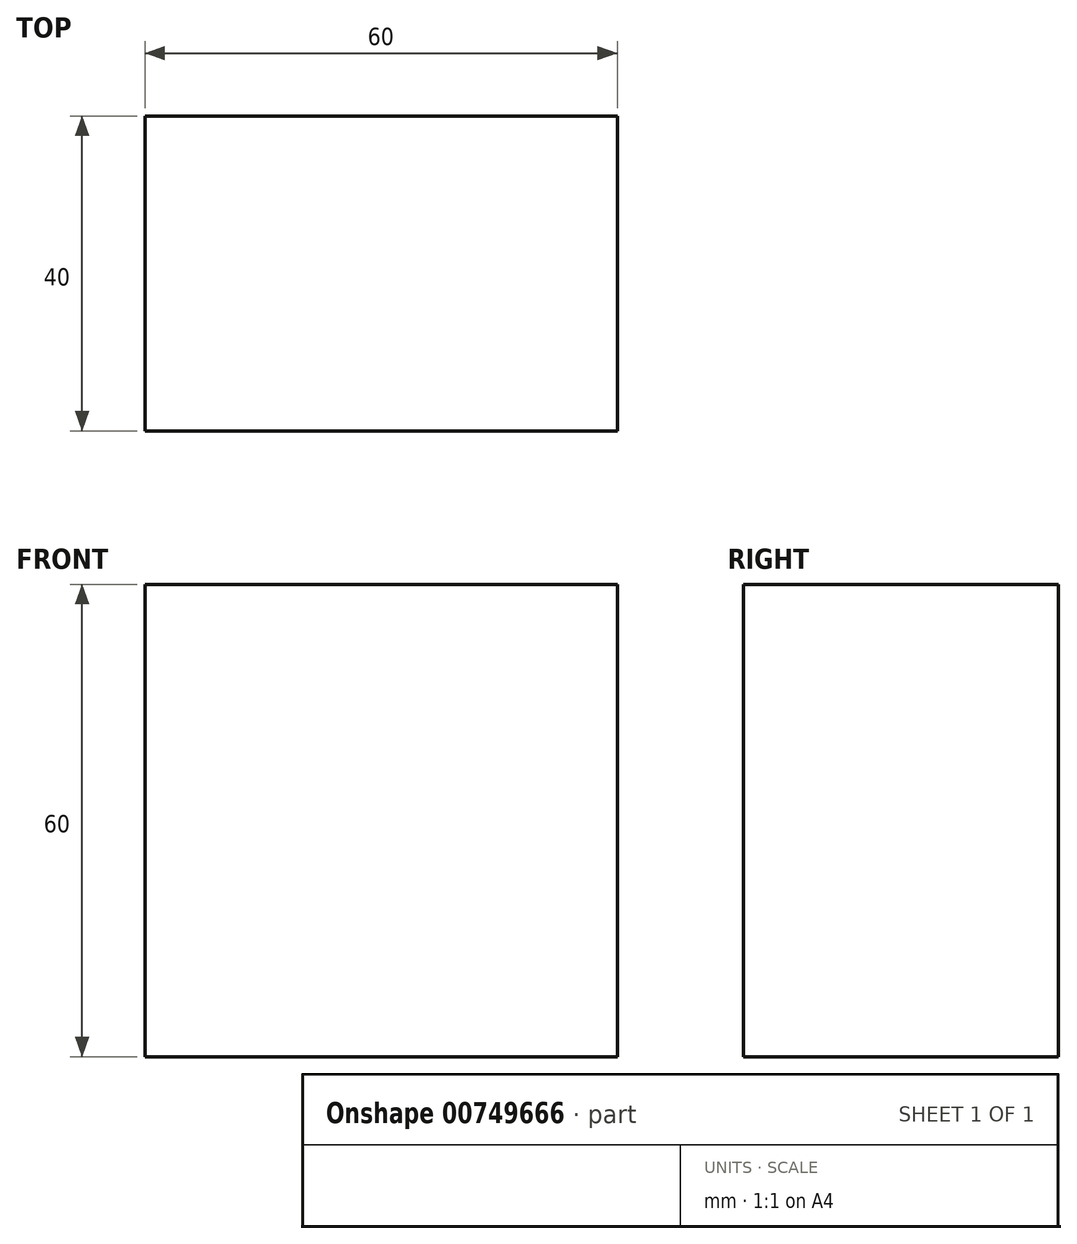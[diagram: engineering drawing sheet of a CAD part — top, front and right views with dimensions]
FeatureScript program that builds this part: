
annotation { "Feature Type Name" : "Feature", "Feature Type Description" : "" }
export const myFeature = defineFeature(function(context is Context, id is Id, definition is map)
    precondition{}
    {
        {
            var Q0;
            Q0=qCreatedBy(makeId("Front.planeOp"),FACE);
            var sketch = newSketch(context, id + "F0", { "sketchPlane" : qUnion([Q0])});
            skLineSegment(sketch, "E0.bottom", {"start": v(0, 0) * mm, "end": v(60, 0) * mm});
            skLineSegment(sketch, "E0.top", {"start": v(0, 60) * mm, "end": v(60, 60) * mm});
            skLineSegment(sketch, "E0.left", {"start": v(0, 0) * mm, "end": v(0, 60) * mm});
            skLineSegment(sketch, "E0.right", {"start": v(60, 0) * mm, "end": v(60, 60) * mm});
            skSolve(sketch);
        }
        {
            var Q0;
            Q0=makeQuery(id+"F0.imprint","IMPRINT",FACE,{"disambiguationData":[TD([[makeQuery(id+"F0.imprint","IMPRINT",EDGE,{"derivedFrom":sQuery(id+"F0.wireOp",EDGE,"E0.bottom")}),1.0]])]});
            extrude(context, id + "F1", {"entities" : qUnion([Q0]), "depth" : 40 * mm, "offsetDistance" : 25 * mm});
        }
    });
